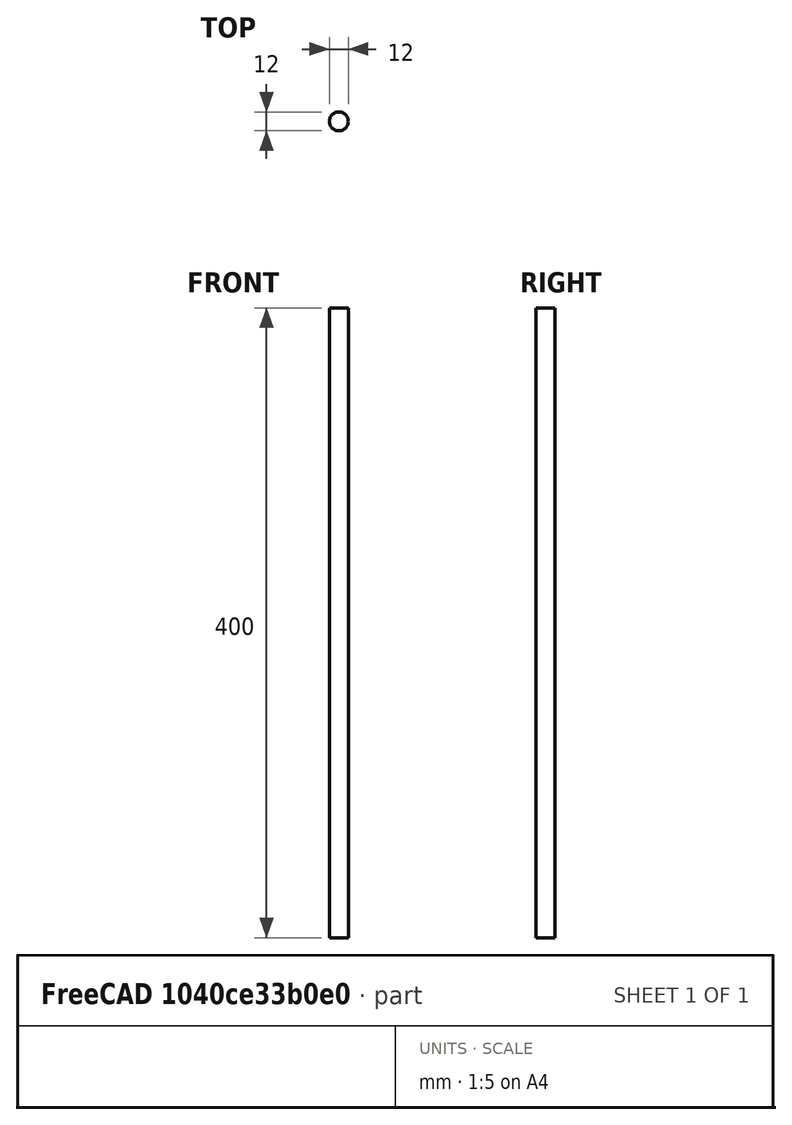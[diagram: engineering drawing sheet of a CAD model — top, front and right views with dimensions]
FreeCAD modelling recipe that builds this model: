
FCSTD DOCUMENT  (FreeCAD 0.21R33771 (Git))
Label: ViteTrapezioT10
License: All rights reserved
LicenseURL: http://en.wikipedia.org/wiki/All_rights_reserved
objects: Sketcher::SketchObject×1, PartDesign::Pad×1, PartDesign::CoordinateSystem×1, PartDesign::Body×1
note: 5 computed .brp shape members not serialized (recipe doc carries the construction recipe); baked Part::Feature solids carry a one-line shape summary decoded from their .brp

FEATURE [Sketcher::SketchObject] Sketch
  FullyConstrained = true
  MapMode = 5
  Support = -> [XY_Plane]
  sketch-geometry (1):
    g0: Circle CenterX=0 CenterY=0 CenterZ=0 NormalX=0 NormalY=0 NormalZ=1 AngleXU=0 Radius=6
  constraints (2):
    c: Coincident(g0,g-1)
    c: Radius(g0) = 6
FEATURE [PartDesign::Pad] Pad
  Direction = (0,0,1)
  Length = 400
  Length2 = 10
  Profile = -> Sketch
  ReferenceAxis = -> Sketch [N_Axis]
  Type = 0
FEATURE [PartDesign::CoordinateSystem] LCS_ViteTrapezioT10
  AttacherType = Attacher::AttachEngine3D
FEATURE [PartDesign::Body] Body  label="Corpo"
  Group = -> [Sketch,Pad,LCS_ViteTrapezioT10]
  Origin = -> Origin
  Tip = -> Pad
